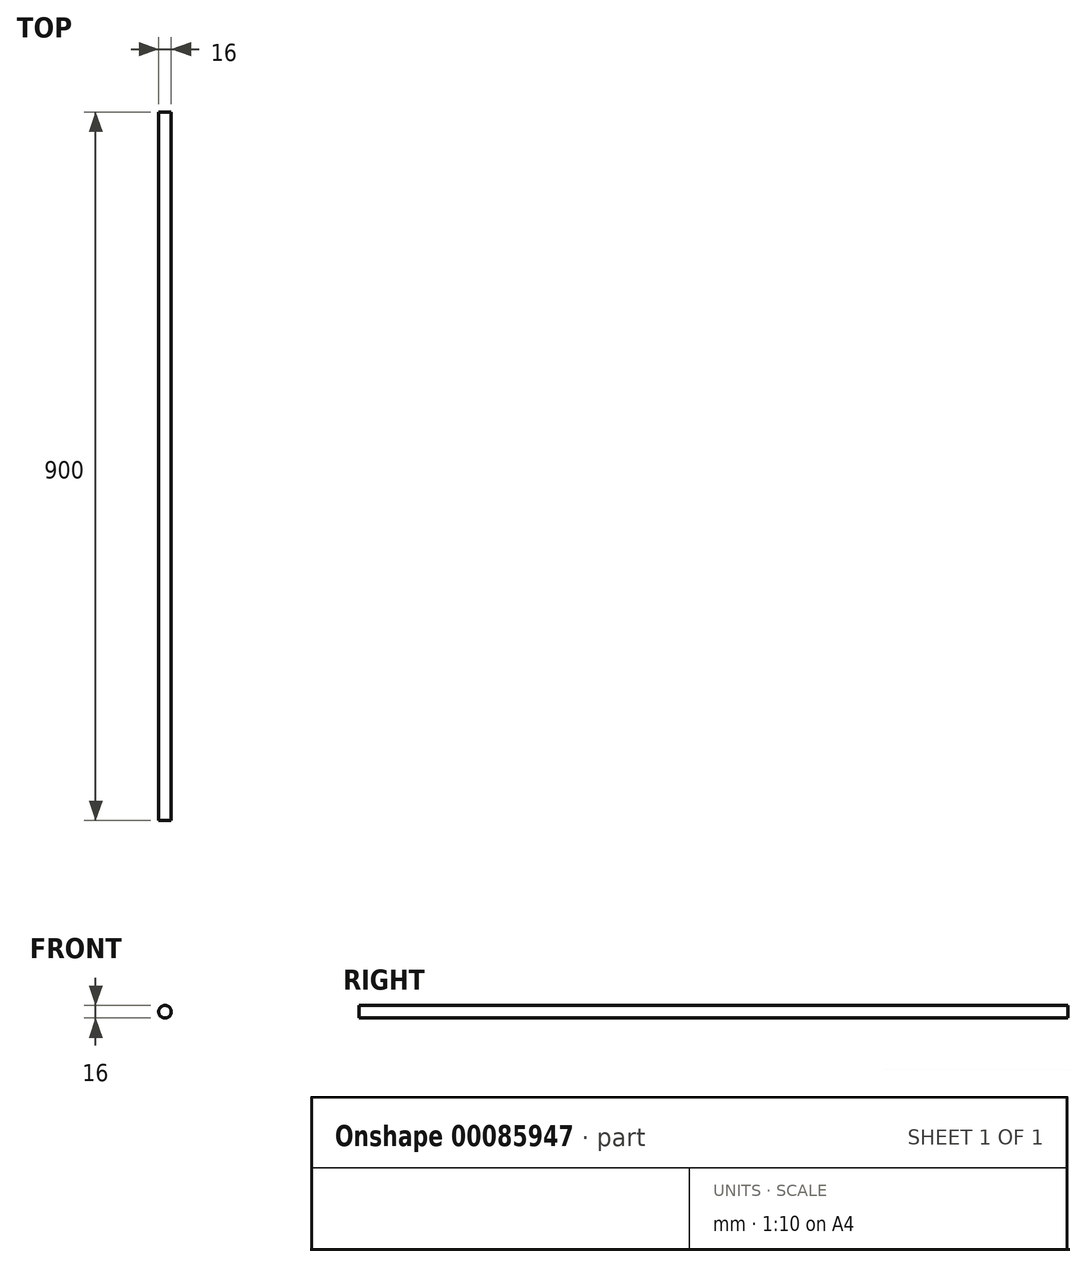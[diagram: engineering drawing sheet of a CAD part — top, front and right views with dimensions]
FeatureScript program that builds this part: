
annotation { "Feature Type Name" : "Feature", "Feature Type Description" : "" }
export const myFeature = defineFeature(function(context is Context, id is Id, definition is map)
    precondition{}
    {
        {
            var Q0;
            Q0=qCreatedBy(makeId("Front.planeOp"),FACE);
            var sketch = newSketch(context, id + "F0", { "sketchPlane" : qUnion([Q0])});
            skCircle(sketch, "E0", {"center": v(-41.8, 38.39) * mm, "radius": 8 * mm});
            skSolve(sketch);
        }
        {
            var Q0;
            Q0=sQuery(id+"F0.wireOp",EDGE,"E0");
            extrude(context, id + "F1", {"bodyType" : ToolBodyType.SURFACE, "surfaceEntities" : qUnion([Q0]), "depth" : 900 * mm});
        }
    });
